# Revit family: RVi-IPC11S
name_source: partatom
category: Устройства связи
revit_build: Autodesk Revit 2016 (Build: 20161004_0715(x64)
units: mm (PartAtom-declared; Revit-internal decimal feet)

## family parameters
Всегда вертикально = Да
На основе рабочей плоскости = Да
Общий = Нет
При загрузке вырезать с полостями = Нет
Размер круглого соединителя = Использовать диаметр
Сохранять ориентацию аннотаций = Нет
Тип детали = Нормальный
Точка расчета площади = Нет

## types (1)
- Стандартная
    2D.Телекамера в герметичном термокожухе = Нет
    2D.Телекамера с поворотным устройством = Нет
    Bullet.корпус = Корпус 11S : Тип
    Bullet.крепление = Корпус 11S.крепление : Тип
    Kr_max = 360.00°
    Kr_min = -360.00°
    RVi.Аудио.Вход = Нет
    RVi.Аудио.Выход = Нет
    RVi.Аудио.Динамик = Да
    RVi.Аудио.Микрофон = Да
    RVi.ИК подсветка.Дальность = 10000 мм
    RVi.Карта памяти = Да
    RVi.Питание 12В = Да
    RVi.Питание 24В = Нет
    RVi.Питание POE = Да
    RVi.Разрешение = 1280×780
    RVi.Тип корпуса = Фиксированные малогабаритные
    RVi.Тип продукта = Камеры внутренней установки
    RVi.Тревога = Да
    RVi.Функция аналитики = Да
    Rn_max = 90.00°
    Rn_min = -90.00°
    Ro_max = 360.00°
    Ro_min = -360.00°
    URL = http://rvi-cctv.ru
    Ug_max = 67.00°
    Ug_min = 66.50°
    Uv_max = 50.00°
    Uv_min = 49.50°
    Вращение всей камеры = 0.00°
    Группа модели = Камера в сборе
    Длина неподвижной части корпуса = 82 мм
    Длина подвижной части = 44 мм
    Изготовитель = RVi
    К идентификации = 250
    К обнаружения = 20
    К распознавания номера = 240
    К распознования = 100
    Крепление = Без крепления : Пусто
    Купол.корпус = Без корпуса : Пусто
    Купол.обектив = Без корпуса : Пусто
    Купольная камера = Нет
    Материал корпуса камеры = Камера.корпус
    Материал крепления = Камера.крепление
    Материал объектива камеры = Камера.объектив
    Наименование и техническая характеристика = Фиксированная малогабаритная IP-камера; 1/4” КМОП;  Формат сжатия: H.264/MJPEG; Максимальное разрешение и скорость трансляции: 1280х720, 25 к/с; Объектив: 2.8 мм; Нижний порог чувствительности: 0.01 лк @ F1.2 цвет / 0.028 лк @ F2 ч.б.; ИК-подсветка: до 10 метров; Встроенный микрофон и динамик; Встроенная видеоаналитика; Тревожный вх./вых.: 1/1;  Запись на MicroSD карту до 128 ГБ;  Питание: PoE / DC 12 В; Диапазон рабочих температур: -10°С...+60°С.
    Обектив коррекция наклона = 90.00°
    Отметка по умолчанию = 1219 мм
    Поворот направления взгляда = 0.00°
    Смещение объектива = 10 мм
    Стрела длина = 0 мм
    Стрела коррекция = 0.00°
    Стрела угол подъема = 0.00°
    УГО смещение = 100 мм
    да = Да
    нет = Нет

## geometry (parser evidence)
native form markers: Blend x12
no freeform markers — native parametric forms only
